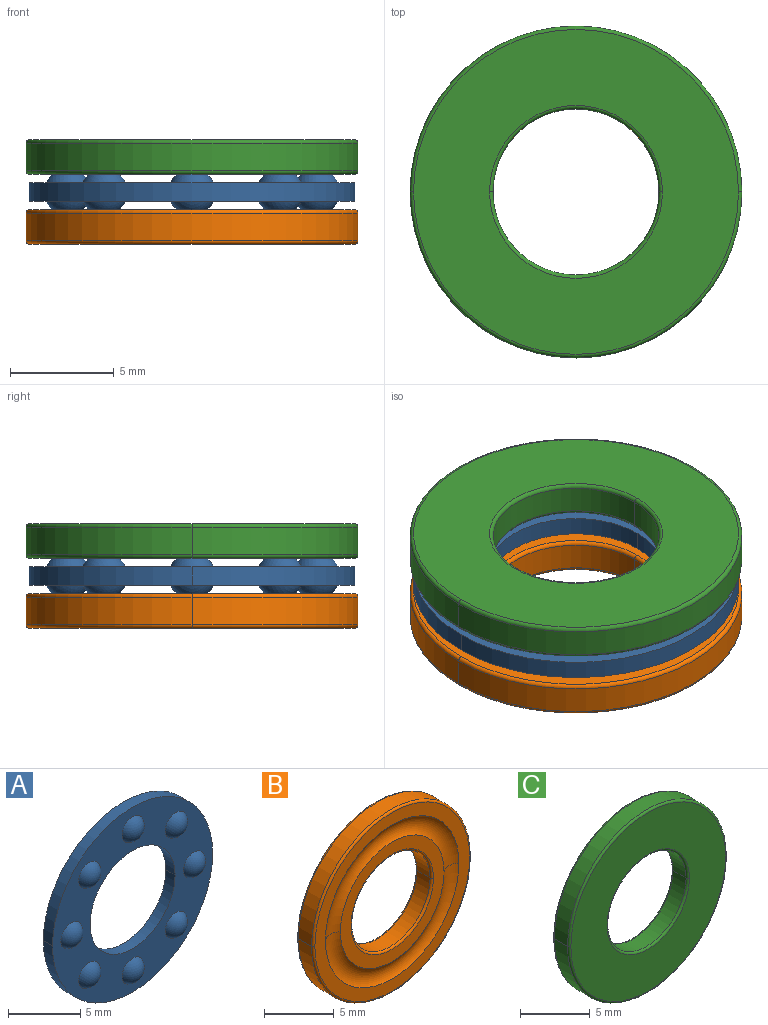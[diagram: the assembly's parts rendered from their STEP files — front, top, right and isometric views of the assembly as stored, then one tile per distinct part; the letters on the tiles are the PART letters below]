
ASSEMBLY  parts=3 mates=4
PART A: 22 faces, bbox 15.7x2.3x15.7 mm
  f0: sphere r=1.12mm, area 4.8mm2, adj f19
  f1: sphere r=1.12mm, area 4.8mm2, adj f19
  f2: sphere r=1.12mm, area 4.8mm2, adj f19
  f3: sphere r=1.12mm, area 4.8mm2, adj f19
  f4: sphere r=1.12mm, area 4.8mm2, adj f19
  f5: sphere r=1.12mm, area 4.8mm2, adj f19
  f6: sphere r=1.12mm, area 4.8mm2, adj f19
  f7: sphere r=1.12mm, area 4.8mm2, adj f19
  f8: sphere r=1.12mm, area 4.8mm2, adj f16
  f9: sphere r=1.12mm, area 4.8mm2, adj f16
  f10: sphere r=1.12mm, area 4.8mm2, adj f16
  f11: sphere r=1.12mm, area 4.8mm2, adj f16
  f12: sphere r=1.12mm, area 4.8mm2, adj f16
  f13: sphere r=1.12mm, area 4.8mm2, adj f16
  f14: sphere r=1.12mm, area 4.8mm2, adj f16
  f15: sphere r=1.12mm, area 4.8mm2, adj f16
  f16: plane 15.68x15.68mm, normal (0,1,0), area 112mm2, adj f8,f9,f10,f11,f12,f13,f14,f15
  f17: cylinder r=4.16mm len=8.32mm, axis (0,-1,0), area 11.8mm2, adj f16,f18,f19
  f18: cylinder r=4.16mm len=8.32mm, axis (0,-1,0), area 11.8mm2, adj f16,f17,f19
  f19: plane 15.68x15.68mm, normal (0,-1,0), area 112mm2, adj f0,f1,f2,f3,f4,f5,f6,f7
  f20: cylinder r=7.84mm len=15.68mm, axis (0,-1,0), area 22.2mm2, adj f16,f19,f21
  f21: cylinder r=7.84mm len=15.68mm, axis (0,-1,0), area 22.2mm2, adj f16,f19,f20
PART B: 306 faces, bbox 17.3x1.7x17.3 mm
  f0: plane 1.01x0.83mm, normal (0,1,0), area 0.3mm2, adj f1,f2,f3,f4,f5,f6,f7,f8
  f1: plane 0.15x0.07mm, normal (0,0,-1), area 0mm2, adj f0,f2,f54,f304
  f2: plane 0.15x0.1mm, normal (-0.31,0,-0.95), area 0mm2, adj f0,f1,f3,f304
  f3: plane 0.15x0.09mm, normal (-0.57,0,-0.82), area 0mm2, adj f0,f2,f4,f304
  f4: plane 0.15x0.09mm, normal (-0.87,0,-0.49), area 0mm2, adj f0,f3,f5,f304
  f5: plane 0.15x0.1mm, normal (-0.95,0,-0.31), area 0mm2, adj f0,f4,f6,f304
  f6: plane 0.15x0.09mm, normal (-1,0,-0.06), area 0mm2, adj f0,f5,f7,f304
  f7: plane 0.15x0.09mm, normal (-0.99,0,0.16), area 0mm2, adj f0,f6,f8,f304
  f8: plane 0.15x0.11mm, normal (-0.89,0,0.46), area 0mm2, adj f0,f7,f9,f304
  f9: plane 0.15x0.07mm, normal (-0.53,0,0.85), area 0mm2, adj f0,f8,f10,f304
  f10: plane 0.15x0.08mm, normal (-0.31,0,0.95), area 0mm2, adj f0,f9,f11,f304
  f11: plane 0.15x0.09mm, normal (-0.07,0,1), area 0mm2, adj f0,f10,f12,f304
  f12: plane 0.15x0.11mm, normal (0.45,0,0.9), area 0mm2, adj f0,f11,f13,f304
  f13: plane 0.15x0.07mm, normal (0.71,0,0.71), area 0mm2, adj f0,f12,f14,f304
  f14: plane 0.15x0.07mm, normal (0.85,0,0.53), area 0mm2, adj f0,f13,f15,f304
  f15: plane 0.15x0.12mm, normal (0.95,0,0.31), area 0mm2, adj f0,f14,f16,f304
  f16: plane 0.15x0.07mm, normal (0.85,0,0.53), area 0mm2, adj f0,f15,f17,f304
  f17: plane 0.15x0.06mm, normal (0.61,0,0.79), area 0mm2, adj f0,f16,f18,f304
  f18: plane 0.15x0.07mm, normal (0.26,0,0.97), area 0mm2, adj f0,f17,f19,f304
  f19: plane 0.15x0.06mm, normal (-0.31,0,0.95), area 0mm2, adj f0,f18,f20,f304
  f20: plane 0.15x0.06mm, normal (-0.78,0,0.63), area 0mm2, adj f0,f19,f21,f304
  f21: plane 0.15x0.07mm, normal (-0.96,0,0.28), area 0mm2, adj f0,f20,f22,f304
  f22: plane 0.15x0.09mm, normal (-1,0,-0.06), area 0mm2, adj f0,f21,f23,f304
  f23: plane 0.16x0.15mm, normal (-0.95,0,-0.31), area 0mm2, adj f0,f22,f24,f304
  f24: plane 0.15x0.07mm, normal (-0.85,0,-0.53), area 0mm2, adj f0,f23,f25,f304
  f25: plane 0.15x0.08mm, normal (-0.45,0,-0.9), area 0mm2, adj f0,f24,f26,f304
  f26: plane 0.15x0.07mm, normal (0,0,-1), area 0mm2, adj f0,f25,f27,f304
  f27: plane 0.15x0.12mm, normal (-0.95,0,-0.31), area 0mm2, adj f0,f26,f28,f304
  f28: plane 0.15x0.09mm, normal (-0.07,0,1), area 0mm2, adj f0,f27,f29,f304
  f29: plane 0.15x0.12mm, normal (0.22,0,0.98), area 0mm2, adj f0,f28,f30,f304
  f30: plane 0.15x0.09mm, normal (0.65,0,0.76), area 0mm2, adj f0,f29,f31,f304
  f31: plane 0.15x0.09mm, normal (0.87,0,0.49), area 0mm2, adj f0,f30,f32,f304
  f32: plane 0.16x0.15mm, normal (0.95,0,0.31), area 0mm2, adj f0,f31,f33,f304
  f33: plane 0.15x0.11mm, normal (0.99,0,0.11), area 0mm2, adj f0,f32,f34,f304
  f34: plane 0.15x0.09mm, normal (0.99,0,-0.16), area 0mm2, adj f0,f33,f35,f304
  f35: plane 0.15x0.11mm, normal (0.89,0,-0.46), area 0mm2, adj f0,f34,f36,f304
  f36: plane 0.15x0.07mm, normal (0.7,0,-0.72), area 0mm2, adj f0,f35,f37,f304
  f37: plane 0.15x0.1mm, normal (0.31,0,-0.95), area 0mm2, adj f0,f36,f38,f304
  f38: plane 0.15x0.09mm, normal (-0.14,0,-0.99), area 0mm2, adj f0,f37,f39,f304
  f39: plane 0.15x0.11mm, normal (-0.45,0,-0.9), area 0mm2, adj f0,f38,f40,f304
  f40: plane 0.15x0.07mm, normal (-0.71,0,-0.71), area 0mm2, adj f0,f39,f41,f304
  f41: plane 0.15x0.09mm, normal (-0.87,0,-0.49), area 0mm2, adj f0,f40,f42,f304
  f42: plane 0.15x0.12mm, normal (-0.95,0,-0.31), area 0mm2, adj f0,f41,f43,f304
  f43: plane 0.15x0.05mm, normal (-0.8,0,-0.6), area 0mm2, adj f0,f42,f44,f304
  f44: plane 0.15x0.06mm, normal (-0.61,0,-0.79), area 0mm2, adj f0,f43,f45,f304
  f45: plane 0.15x0.07mm, normal (0,0,-1), area 0mm2, adj f0,f44,f46,f304
  f46: plane 0.15x0.04mm, normal (0.31,0,-0.95), area 0mm2, adj f0,f45,f47,f304
  f47: plane 0.15x0.05mm, normal (0.59,0,-0.81), area 0mm2, adj f0,f46,f48,f304
  f48: plane 0.15x0.07mm, normal (0.96,0,-0.28), area 0mm2, adj f0,f47,f49,f304
  f49: plane 0.15x0.07mm, normal (1,0,-0.01), area 0mm2, adj f0,f48,f50,f304
  f50: plane 0.15x0.12mm, normal (0.95,0,0.31), area 0mm2, adj f0,f49,f51,f304
  f51: plane 0.15x0.05mm, normal (0.8,0,0.6), area 0mm2, adj f0,f50,f52,f304
  f52: plane 0.15x0.05mm, normal (0.45,0,0.9), area 0mm2, adj f0,f51,f53,f304
  f53: plane 0.15x0.05mm, normal (0.14,0,0.99), area 0mm2, adj f0,f52,f54,f304
  f54: plane 0.15x0.12mm, normal (0.95,0,0.31), area 0mm2, adj f0,f1,f53,f304
  f55: plane 0.31x0.15mm, normal (-0.99,0,-0.14), area 0mm2, adj f56,f60,f98,f304
  f56: plane 0.15x0.13mm, normal (-0.14,0,0.99), area 0mm2, adj f55,f57,f60,f304
  f57: plane 0.19x0.15mm, normal (0.99,0,0.14), area 0mm2, adj f56,f58,f60,f304
  f58: plane 0.17x0.15mm, normal (-0.14,0,0.99), area 0mm2, adj f57,f59,f60,f304
  f59: plane 0.15x0.06mm, normal (-0.44,0,0.9), area 0mm2, adj f58,f60,f304,f305
  f60: plane 1.02x0.86mm, normal (0,1,0), area 0.3mm2, adj f55,f56,f57,f58,f59,f61,f62,f63
  f61: plane 0.15x0.09mm, normal (-0.99,0,0.11), area 0mm2, adj f60,f62,f304,f305
  f62: plane 0.19x0.15mm, normal (-0.99,0,-0.14), area 0mm2, adj f60,f61,f63,f304
  f63: plane 0.15x0.08mm, normal (-0.93,0,-0.38), area 0mm2, adj f60,f62,f64,f304
  f64: plane 0.15x0.06mm, normal (-0.74,0,-0.67), area 0mm2, adj f60,f63,f65,f304
  f65: plane 0.15x0.07mm, normal (-0.42,0,-0.91), area 0mm2, adj f60,f64,f66,f304
  f66: plane 0.15x0.09mm, normal (-0.1,0,-0.99), area 0mm2, adj f60,f65,f67,f304
  f67: plane 0.32x0.15mm, normal (0.14,0,-0.99), area 0mm2, adj f60,f66,f68,f304
  f68: plane 0.15x0.08mm, normal (0.37,0,-0.93), area 0mm2, adj f60,f67,f69,f304
  f69: plane 0.15x0.06mm, normal (0.66,0,-0.75), area 0mm2, adj f60,f68,f70,f304
  f70: plane 0.15x0.07mm, normal (0.9,0,-0.44), area 0mm2, adj f60,f69,f71,f304
  f71: plane 0.15x0.09mm, normal (0.99,0,-0.11), area 0mm2, adj f60,f70,f72,f304
  f72: plane 0.19x0.15mm, normal (0.99,0,0.14), area 0mm2, adj f60,f71,f73,f304
  f73: plane 0.15x0.08mm, normal (0.93,0,0.38), area 0mm2, adj f60,f72,f74,f304
  f74: plane 0.15x0.06mm, normal (0.74,0,0.67), area 0mm2, adj f60,f73,f75,f304
  f75: plane 0.15x0.07mm, normal (0.18,0,0.98), area 0mm2, adj f60,f74,f76,f304
  f76: plane 0.15x0.12mm, normal (0.99,0,0.14), area 0mm2, adj f60,f75,f77,f304
  f77: plane 0.15x0.11mm, normal (-0.05,0,-1), area 0mm2, adj f60,f76,f78,f304
  f78: plane 0.15x0.1mm, normal (-0.59,0,-0.8), area 0mm2, adj f60,f77,f79,f304
  f79: plane 0.15x0.08mm, normal (-0.82,0,-0.57), area 0mm2, adj f60,f78,f80,f304
  f80: plane 0.15x0.1mm, normal (-0.94,0,-0.33), area 0mm2, adj f60,f79,f81,f304
  f81: plane 0.19x0.15mm, normal (-0.99,0,-0.14), area 0mm2, adj f60,f80,f82,f304
  f82: plane 0.15x0.11mm, normal (-1,0,0.06), area 0mm2, adj f60,f81,f83,f304
  f83: plane 0.15x0.09mm, normal (-0.95,0,0.33), area 0mm2, adj f60,f82,f84,f304
  f84: plane 0.15x0.09mm, normal (-0.79,0,0.61), area 0mm2, adj f60,f83,f85,f304
  f85: plane 0.15x0.08mm, normal (-0.56,0,0.83), area 0mm2, adj f60,f84,f86,f304
  f86: plane 0.15x0.1mm, normal (-0.33,0,0.95), area 0mm2, adj f60,f85,f87,f304
  f87: plane 0.32x0.15mm, normal (-0.14,0,0.99), area 0mm2, adj f60,f86,f88,f304
  f88: plane 0.15x0.11mm, normal (0.05,0,1), area 0mm2, adj f60,f87,f89,f304
  f89: plane 0.15x0.09mm, normal (0.31,0,0.95), area 0mm2, adj f60,f88,f90,f304
  f90: plane 0.15x0.1mm, normal (0.59,0,0.8), area 0mm2, adj f60,f89,f91,f304
  f91: plane 0.15x0.08mm, normal (0.82,0,0.57), area 0mm2, adj f60,f90,f92,f304
  f92: plane 0.15x0.1mm, normal (0.94,0,0.33), area 0mm2, adj f60,f91,f93,f304
  f93: plane 0.19x0.15mm, normal (0.99,0,0.14), area 0mm2, adj f60,f92,f94,f304
  f94: plane 0.15x0.11mm, normal (1,0,-0.06), area 0mm2, adj f60,f93,f95,f304
  f95: plane 0.15x0.09mm, normal (0.95,0,-0.33), area 0mm2, adj f60,f94,f96,f304
  f96: plane 0.15x0.09mm, normal (0.79,0,-0.61), area 0mm2, adj f60,f95,f97,f304
  f97: plane 0.15x0.08mm, normal (0.37,0,-0.93), area 0mm2, adj f60,f96,f98,f304
  f98: plane 0.32x0.15mm, normal (0.14,0,-0.99), area 0mm2, adj f55,f60,f97,f304
  f99: plane 1.03x0.87mm, normal (0,1,0), area 0.4mm2, adj f100,f101,f102,f103,f104,f105,f106,f107
  f100: plane 0.85x0.56mm, normal (0.55,0,0.84), area 0.2mm2, adj f99,f101,f109,f304
  f101: plane 0.19x0.15mm, normal (1,0,-0.04), area 0mm2, adj f99,f100,f102,f304
  f102: plane 1x0.15mm, normal (-0.04,0,-1), area 0.1mm2, adj f99,f101,f103,f304
  f103: plane 0.15x0.13mm, normal (-1,0,0.04), area 0mm2, adj f99,f102,f104,f304
  f104: plane 0.85x0.15mm, normal (0.04,0,1), area 0.1mm2, adj f99,f103,f105,f304
  f105: plane 0.83x0.56mm, normal (-0.56,0,-0.83), area 0.1mm2, adj f99,f104,f106,f304
  f106: plane 0.19x0.15mm, normal (-1,0,0.04), area 0mm2, adj f99,f105,f107,f304
  f107: plane 1x0.15mm, normal (0.04,0,1), area 0.1mm2, adj f99,f106,f108,f304
  f108: plane 0.15x0.13mm, normal (1,0,-0.04), area 0mm2, adj f99,f107,f109,f304
  f109: plane 0.87x0.15mm, normal (-0.04,0,-1), area 0.1mm2, adj f99,f100,f108,f304
  f110: plane 1.01x0.28mm, normal (0,1,0), area 0.1mm2, adj f111,f112,f113,f114
  f111: plane 0.15x0.12mm, normal (-0.99,0,0.16), area 0mm2, adj f110,f112,f114,f304
  f112: plane 0.99x0.16mm, normal (0.16,0,0.99), area 0.2mm2, adj f110,f111,f113,f304
  f113: plane 0.15x0.12mm, normal (0.99,0,-0.16), area 0mm2, adj f110,f112,f114,f304
  f114: plane 0.99x0.16mm, normal (-0.16,0,-0.99), area 0.2mm2, adj f110,f111,f113,f304
  f115: plane 0.15x0.05mm, normal (-0.83,0,0.56), area 0mm2, adj f116,f124,f125,f126
  f116: plane 0.15x0.05mm, normal (-0.48,0,0.88), area 0mm2, adj f115,f117,f124,f126
  f117: plane 0.15x0.07mm, normal (-0.04,0,1), area 0mm2, adj f116,f118,f124,f126
  f118: plane 0.15x0.06mm, normal (0.27,0,0.96), area 0mm2, adj f117,f119,f124,f126
  f119: plane 0.15x0.06mm, normal (0.55,0,0.83), area 0mm2, adj f118,f120,f124,f126
  f120: plane 0.15x0.05mm, normal (0.87,0,0.5), area 0mm2, adj f119,f121,f124,f126
  f121: plane 0.15x0.07mm, normal (1,0,0.06), area 0mm2, adj f120,f122,f124,f126
  f122: plane 0.38x0.15mm, normal (0.96,0,-0.27), area 0.1mm2, adj f121,f123,f124,f126
  f123: plane 0.31x0.15mm, normal (-0.27,0,-0.96), area 0mm2, adj f122,f124,f125,f126
  f124: plane 0.55x0.41mm, normal (0,1,0), area 0.2mm2, adj f115,f116,f117,f118,f119,f120,f121,f122
  f125: plane 0.38x0.15mm, normal (-0.96,0,0.27), area 0.1mm2, adj f115,f123,f124,f126
  f126: plane 1.11x1.03mm, normal (0,1,0), area 0.4mm2, adj f115,f116,f117,f118,f119,f120,f121,f122
  f127: plane 0.39x0.28mm, normal (0.59,0,0.81), area 0.1mm2, adj f126,f128,f142,f304
  f128: plane 0.15x0.14mm, normal (0.96,0,-0.27), area 0mm2, adj f126,f127,f129,f304
  f129: plane 0.42x0.31mm, normal (-0.6,0,-0.8), area 0.1mm2, adj f126,f128,f130,f304
  f130: plane 0.15x0.07mm, normal (0.74,0,-0.68), area 0mm2, adj f126,f129,f131,f304
  f131: plane 0.15x0.1mm, normal (0.35,0,-0.94), area 0mm2, adj f126,f130,f132,f304
  f132: plane 0.15x0.07mm, normal (0.04,0,-1), area 0mm2, adj f126,f131,f133,f304
  f133: plane 0.15x0.08mm, normal (-0.27,0,-0.96), area 0mm2, adj f126,f132,f134,f304
  f134: plane 0.15x0.06mm, normal (-0.55,0,-0.83), area 0mm2, adj f126,f133,f135,f304
  f135: plane 0.15x0.08mm, normal (-0.79,0,-0.62), area 0mm2, adj f126,f134,f136,f304
  f136: plane 0.15x0.1mm, normal (-0.93,0,-0.37), area 0mm2, adj f126,f135,f137,f304
  f137: plane 0.15x0.11mm, normal (-1,0,0.07), area 0mm2, adj f126,f136,f138,f304
  f138: plane 0.48x0.15mm, normal (-0.96,0,0.27), area 0.1mm2, adj f126,f137,f139,f304
  f139: plane 0.96x0.27mm, normal (0.27,0,0.96), area 0.1mm2, adj f126,f138,f140,f304
  f140: plane 0.15x0.12mm, normal (0.96,0,-0.27), area 0mm2, adj f126,f139,f141,f304
  f141: plane 0.43x0.15mm, normal (-0.27,0,-0.96), area 0.1mm2, adj f126,f140,f142,f304
  f142: plane 0.34x0.15mm, normal (0.96,0,-0.27), area 0.1mm2, adj f126,f127,f141,f304
  f143: plane 0.6x0.15mm, normal (-0.13,0,-0.99), area 0.1mm2, adj f144,f145,f146,f147
  f144: plane 0.34x0.16mm, normal (-0.9,0,0.43), area 0.1mm2, adj f143,f145,f146,f147
  f145: plane 0.6x0.42mm, normal (0,1,0), area 0.1mm2, adj f143,f144,f146
  f146: plane 0.44x0.42mm, normal (0.69,0,0.72), area 0.1mm2, adj f143,f144,f145,f147
  f147: plane 1.12x0.89mm, normal (0,1,0), area 0.3mm2, adj f143,f144,f146,f148,f149,f150,f151,f152
  f148: plane 1.05x0.15mm, normal (0.13,0,0.99), area 0.2mm2, adj f147,f149,f155,f304
  f149: plane 0.15x0.11mm, normal (0.9,0,-0.43), area 0mm2, adj f147,f148,f150,f304
  f150: plane 0.27x0.15mm, normal (-0.13,0,-0.99), area 0mm2, adj f147,f149,f151,f304
  f151: plane 0.38x0.18mm, normal (0.9,0,-0.43), area 0.1mm2, adj f147,f150,f152,f304
  f152: plane 0.19x0.19mm, normal (0.69,0,0.72), area 0mm2, adj f147,f151,f153,f304
  f153: plane 0.15x0.11mm, normal (0.9,0,-0.43), area 0mm2, adj f147,f152,f154,f304
  f154: plane 0.76x0.74mm, normal (-0.7,0,-0.72), area 0.2mm2, adj f147,f153,f155,f304
  f155: plane 0.15x0.15mm, normal (-0.9,0,0.43), area 0mm2, adj f147,f148,f154,f304
  f156: plane 1.25x1.19mm, normal (0,1,0), area 0.4mm2, adj f157,f158,f159,f160,f161,f162,f163,f164
  f157: plane 0.28x0.2mm, normal (-0.58,0,-0.81), area 0.1mm2, adj f156,f158,f168,f304
  f158: plane 0.44x0.32mm, normal (0.81,0,-0.58), area 0.1mm2, adj f156,f157,f159,f304
  f159: plane 0.15x0.1mm, normal (-0.58,0,-0.81), area 0mm2, adj f156,f158,f160,f304
  f160: plane 0.44x0.32mm, normal (-0.81,0,0.58), area 0.1mm2, adj f156,f159,f161,f304
  f161: plane 0.22x0.16mm, normal (-0.58,0,-0.81), area 0mm2, adj f156,f160,f162,f304
  f162: plane 0.51x0.37mm, normal (0.81,0,-0.58), area 0.1mm2, adj f156,f161,f163,f304
  f163: plane 0.15x0.1mm, normal (-0.58,0,-0.81), area 0mm2, adj f156,f162,f164,f304
  f164: plane 0.61x0.44mm, normal (-0.81,0,0.58), area 0.1mm2, adj f156,f163,f165,f304
  f165: plane 0.81x0.58mm, normal (0.58,0,0.81), area 0.2mm2, adj f156,f164,f166,f304
  f166: plane 0.61x0.44mm, normal (0.81,0,-0.58), area 0.1mm2, adj f156,f165,f167,f304
  f167: plane 0.15x0.1mm, normal (-0.58,0,-0.81), area 0mm2, adj f156,f166,f168,f304
  f168: plane 0.51x0.37mm, normal (-0.81,0,0.58), area 0.1mm2, adj f156,f157,f167,f304
  f169: plane 0.15x0.06mm, normal (0.89,0,0.45), area 0mm2, adj f170,f178,f179,f191
  f170: plane 0.15x0.06mm, normal (1,0,0), area 0mm2, adj f169,f171,f178,f191
  f171: plane 0.15x0.06mm, normal (0.89,0,-0.45), area 0mm2, adj f170,f172,f178,f191
  f172: plane 0.28x0.28mm, normal (0.7,0,-0.71), area 0.1mm2, adj f171,f173,f178,f191
  f173: plane 0.23x0.22mm, normal (-0.71,0,-0.7), area 0mm2, adj f172,f174,f178,f191
  f174: plane 0.28x0.28mm, normal (-0.7,0,0.71), area 0.1mm2, adj f173,f175,f178,f191
  f175: plane 0.15x0.06mm, normal (-0.44,0,0.9), area 0mm2, adj f174,f176,f178,f191
  f176: plane 0.15x0.06mm, normal (0.02,0,1), area 0mm2, adj f175,f177,f178,f191
  f177: plane 0.15x0.06mm, normal (0.46,0,0.89), area 0mm2, adj f176,f178,f179,f191
  f178: plane 0.54x0.53mm, normal (0,1,0), area 0.2mm2, adj f169,f170,f171,f172,f173,f174,f175,f176
  f179: plane 0.15x0.05mm, normal (0.71,0,0.7), area 0mm2, adj f169,f177,f178,f191
  f180: plane 0.21x0.21mm, normal (-0.71,0,-0.7), area 0mm2, adj f181,f189,f190,f191
  f181: plane 0.28x0.28mm, normal (-0.7,0,0.71), area 0.1mm2, adj f180,f182,f189,f191
  f182: plane 0.15x0.06mm, normal (-0.44,0,0.9), area 0mm2, adj f181,f183,f189,f191
  f183: plane 0.15x0.06mm, normal (0.02,0,1), area 0mm2, adj f182,f184,f189,f191
  f184: plane 0.15x0.06mm, normal (0.46,0,0.89), area 0mm2, adj f183,f185,f189,f191
  f185: plane 0.15x0.03mm, normal (0.71,0,0.7), area 0mm2, adj f184,f186,f189,f191
  f186: plane 0.15x0.06mm, normal (0.89,0,0.45), area 0mm2, adj f185,f187,f189,f191
  f187: plane 0.15x0.06mm, normal (1,0,0), area 0mm2, adj f186,f188,f189,f191
  f188: plane 0.15x0.06mm, normal (0.89,0,-0.45), area 0mm2, adj f187,f189,f190,f191
  f189: plane 0.52x0.52mm, normal (0,1,0), area 0.1mm2, adj f180,f181,f182,f183,f184,f185,f186,f187
  f190: plane 0.28x0.28mm, normal (0.7,0,-0.71), area 0.1mm2, adj f180,f188,f189,f191
  f191: plane 1.13x1.13mm, normal (0,1,0), area 0.4mm2, adj f169,f170,f171,f172,f173,f174,f175,f176
  f192: plane 0.15x0.1mm, normal (-0.16,0,-0.99), area 0mm2, adj f191,f193,f210,f304
  f193: plane 0.15x0.06mm, normal (-0.46,0,-0.89), area 0mm2, adj f191,f192,f194,f304
  f194: plane 0.15x0.06mm, normal (-0.71,0,-0.7), area 0mm2, adj f191,f193,f195,f304
  f195: plane 0.15x0.06mm, normal (-0.89,0,-0.45), area 0mm2, adj f191,f194,f196,f304
  f196: plane 0.15x0.1mm, normal (-0.99,0,-0.14), area 0mm2, adj f191,f195,f197,f304
  f197: plane 0.15x0.1mm, normal (-0.99,0,0.14), area 0mm2, adj f191,f196,f198,f304
  f198: plane 0.15x0.09mm, normal (-0.83,0,0.56), area 0mm2, adj f191,f197,f199,f304
  f199: plane 0.36x0.35mm, normal (-0.7,0,0.71), area 0.1mm2, adj f191,f198,f200,f304
  f200: plane 0.71x0.7mm, normal (0.71,0,0.7), area 0.1mm2, adj f191,f199,f201,f304
  f201: plane 0.36x0.35mm, normal (0.7,0,-0.71), area 0.1mm2, adj f191,f200,f202,f304
  f202: plane 0.15x0.09mm, normal (0.55,0,-0.84), area 0mm2, adj f191,f201,f203,f304
  f203: plane 0.15x0.1mm, normal (0.12,0,-0.99), area 0mm2, adj f191,f202,f204,f304
  f204: plane 0.15x0.1mm, normal (-0.16,0,-0.99), area 0mm2, adj f191,f203,f205,f304
  f205: plane 0.15x0.06mm, normal (-0.46,0,-0.89), area 0mm2, adj f191,f204,f206,f304
  f206: plane 0.15x0.08mm, normal (-0.71,0,-0.7), area 0mm2, adj f191,f205,f207,f304
  f207: plane 0.15x0.06mm, normal (-0.89,0,-0.45), area 0mm2, adj f191,f206,f208,f304
  f208: plane 0.15x0.1mm, normal (-0.99,0,-0.14), area 0mm2, adj f191,f207,f209,f304
  f209: plane 0.15x0.04mm, normal (-0.95,0,0.31), area 0mm2, adj f191,f208,f210,f304
  f210: plane 0.15x0.04mm, normal (0.3,0,-0.95), area 0mm2, adj f191,f192,f209,f304
  f211: plane 1.1x0.83mm, normal (0,1,0), area 0.2mm2, adj f212,f213,f214,f215,f216,f217,f218,f219
  f212: plane 0.15x0.1mm, normal (0.91,0,0.41), area 0mm2, adj f211,f213,f219,f304
  f213: plane 0.3x0.15mm, normal (0.41,0,-0.91), area 0mm2, adj f211,f212,f214,f304
  f214: plane 0.81x0.37mm, normal (0.91,0,0.41), area 0.1mm2, adj f211,f213,f215,f304
  f215: plane 0.15x0.11mm, normal (0.41,0,-0.91), area 0mm2, adj f211,f214,f216,f304
  f216: plane 0.81x0.37mm, normal (-0.91,0,-0.41), area 0.1mm2, adj f211,f215,f217,f304
  f217: plane 0.3x0.15mm, normal (0.41,0,-0.91), area 0.1mm2, adj f211,f216,f218,f304
  f218: plane 0.15x0.1mm, normal (-0.91,0,-0.41), area 0mm2, adj f211,f217,f219,f304
  f219: plane 0.72x0.33mm, normal (-0.41,0,0.91), area 0.1mm2, adj f211,f212,f218,f304
  f220: plane 1.01x0.81mm, normal (0,1,0), area 0.3mm2, adj f221,f222,f223,f224,f225,f226,f227,f228
  f221: plane 0.15x0.07mm, normal (-1,0,0.06), area 0mm2, adj f220,f222,f274,f304
  f222: plane 0.15x0.1mm, normal (-0.93,0,0.37), area 0mm2, adj f220,f221,f223,f304
  f223: plane 0.15x0.08mm, normal (-0.79,0,0.62), area 0mm2, adj f220,f222,f224,f304
  f224: plane 0.15x0.1mm, normal (-0.44,0,0.9), area 0mm2, adj f220,f223,f225,f304
  f225: plane 0.15x0.1mm, normal (-0.25,0,0.97), area 0mm2, adj f220,f224,f226,f304
  f226: plane 0.15x0.09mm, normal (0,0,1), area 0mm2, adj f220,f225,f227,f304
  f227: plane 0.15x0.09mm, normal (0.22,0,0.98), area 0mm2, adj f220,f226,f228,f304
  f228: plane 0.15x0.1mm, normal (0.52,0,0.86), area 0mm2, adj f220,f227,f229,f304
  f229: plane 0.15x0.08mm, normal (0.88,0,0.47), area 0mm2, adj f220,f228,f230,f304
  f230: plane 0.15x0.08mm, normal (0.97,0,0.25), area 0mm2, adj f220,f229,f231,f304
  f231: plane 0.15x0.09mm, normal (1,0,0.01), area 0mm2, adj f220,f230,f232,f304
  f232: plane 0.15x0.1mm, normal (0.87,0,-0.5), area 0mm2, adj f220,f231,f233,f304
  f233: plane 0.15x0.07mm, normal (0.66,0,-0.75), area 0mm2, adj f220,f232,f234,f304
  f234: plane 0.15x0.08mm, normal (0.48,0,-0.88), area 0mm2, adj f220,f233,f235,f304
  f235: plane 0.15x0.12mm, normal (0.25,0,-0.97), area 0mm2, adj f220,f234,f236,f304
  f236: plane 0.15x0.08mm, normal (0.48,0,-0.88), area 0mm2, adj f220,f235,f237,f304
  f237: plane 0.15x0.06mm, normal (0.75,0,-0.66), area 0mm2, adj f220,f236,f238,f304
  f238: plane 0.15x0.07mm, normal (0.95,0,-0.32), area 0mm2, adj f220,f237,f239,f304
  f239: plane 0.15x0.06mm, normal (0.97,0,0.25), area 0mm2, adj f220,f238,f240,f304
  f240: plane 0.15x0.06mm, normal (0.67,0,0.74), area 0mm2, adj f220,f239,f241,f304
  f241: plane 0.15x0.07mm, normal (0.34,0,0.94), area 0mm2, adj f220,f240,f242,f304
  f242: plane 0.15x0.09mm, normal (0,0,1), area 0mm2, adj f220,f241,f243,f304
  f243: plane 0.16x0.15mm, normal (-0.25,0,0.97), area 0mm2, adj f220,f242,f244,f304
  f244: plane 0.15x0.08mm, normal (-0.48,0,0.88), area 0mm2, adj f220,f243,f245,f304
  f245: plane 0.15x0.08mm, normal (-0.87,0,0.5), area 0mm2, adj f220,f244,f246,f304
  f246: plane 0.15x0.07mm, normal (-1,0,0.06), area 0mm2, adj f220,f245,f247,f304
  f247: plane 0.15x0.12mm, normal (-0.25,0,0.97), area 0mm2, adj f220,f246,f248,f304
  f248: plane 0.15x0.09mm, normal (1,0,0.01), area 0mm2, adj f220,f247,f249,f304
  f249: plane 0.15x0.12mm, normal (0.96,0,-0.28), area 0mm2, adj f220,f248,f250,f304
  f250: plane 0.15x0.09mm, normal (0.72,0,-0.7), area 0mm2, adj f220,f249,f251,f304
  f251: plane 0.15x0.1mm, normal (0.44,0,-0.9), area 0mm2, adj f220,f250,f252,f304
  f252: plane 0.16x0.15mm, normal (0.25,0,-0.97), area 0mm2, adj f220,f251,f253,f304
  f253: plane 0.15x0.11mm, normal (0.05,0,-1), area 0mm2, adj f220,f252,f254,f304
  f254: plane 0.15x0.09mm, normal (-0.22,0,-0.98), area 0mm2, adj f220,f253,f255,f304
  f255: plane 0.15x0.1mm, normal (-0.52,0,-0.86), area 0mm2, adj f220,f254,f256,f304
  f256: plane 0.15x0.07mm, normal (-0.76,0,-0.65), area 0mm2, adj f220,f255,f257,f304
  f257: plane 0.15x0.1mm, normal (-0.97,0,-0.25), area 0mm2, adj f220,f256,f258,f304
  f258: plane 0.15x0.09mm, normal (-0.98,0,0.2), area 0mm2, adj f220,f257,f259,f304
  f259: plane 0.15x0.1mm, normal (-0.87,0,0.5), area 0mm2, adj f220,f258,f260,f304
  f260: plane 0.15x0.07mm, normal (-0.66,0,0.75), area 0mm2, adj f220,f259,f261,f304
  f261: plane 0.15x0.1mm, normal (-0.44,0,0.9), area 0mm2, adj f220,f260,f262,f304
  f262: plane 0.15x0.12mm, normal (-0.25,0,0.97), area 0mm2, adj f220,f261,f263,f304
  f263: plane 0.15x0.06mm, normal (-0.55,0,0.84), area 0mm2, adj f220,f262,f264,f304
  f264: plane 0.15x0.06mm, normal (-0.75,0,0.66), area 0mm2, adj f220,f263,f265,f304
  f265: plane 0.15x0.07mm, normal (-1,0,0.06), area 0mm2, adj f220,f264,f266,f304
  f266: plane 0.15x0.04mm, normal (-0.97,0,-0.25), area 0mm2, adj f220,f265,f267,f304
  f267: plane 0.15x0.06mm, normal (-0.84,0,-0.54), area 0mm2, adj f220,f266,f268,f304
  f268: plane 0.15x0.07mm, normal (-0.34,0,-0.94), area 0mm2, adj f220,f267,f269,f304
  f269: plane 0.15x0.07mm, normal (-0.08,0,-1), area 0mm2, adj f220,f268,f270,f304
  f270: plane 0.15x0.12mm, normal (0.25,0,-0.97), area 0mm2, adj f220,f269,f271,f304
  f271: plane 0.15x0.06mm, normal (0.55,0,-0.84), area 0mm2, adj f220,f270,f272,f304
  f272: plane 0.15x0.05mm, normal (0.87,0,-0.5), area 0mm2, adj f220,f271,f273,f304
  f273: plane 0.15x0.05mm, normal (0.98,0,-0.2), area 0mm2, adj f220,f272,f274,f304
  f274: plane 0.15x0.12mm, normal (0.25,0,-0.97), area 0mm2, adj f220,f221,f273,f304
  f275: plane 0.56x0.23mm, normal (-0.92,0,-0.38), area 0.1mm2, adj f276,f277,f278,f279
  f276: plane 0.37x0.15mm, normal (-0.08,0,1), area 0.1mm2, adj f275,f277,f278,f279
  f277: plane 0.59x0.37mm, normal (0,1,0), area 0.1mm2, adj f275,f276,f278
  f278: plane 0.59x0.15mm, normal (0.97,0,-0.24), area 0.1mm2, adj f275,f276,f277,f279
  f279: plane 1.04x0.83mm, normal (0,1,0), area 0.3mm2, adj f275,f276,f278,f280,f281,f282,f283,f284
  f280: plane 0.97x0.41mm, normal (0.92,0,0.39), area 0.2mm2, adj f279,f281,f287,f304
  f281: plane 0.15x0.12mm, normal (0.08,0,-1), area 0mm2, adj f279,f280,f282,f304
  f282: plane 0.25x0.15mm, normal (-0.92,0,-0.38), area 0mm2, adj f279,f281,f283,f304
  f283: plane 0.42x0.15mm, normal (0.08,0,-1), area 0.1mm2, adj f279,f282,f284,f304
  f284: plane 0.26x0.15mm, normal (0.97,0,-0.24), area 0mm2, adj f279,f283,f285,f304
  f285: plane 0.15x0.12mm, normal (0.08,0,-1), area 0mm2, adj f279,f284,f286,f304
  f286: plane 1.02x0.26mm, normal (-0.97,0,0.24), area 0.2mm2, adj f279,f285,f287,f304
  f287: plane 0.17x0.15mm, normal (-0.08,0,1), area 0mm2, adj f279,f280,f286,f304
  f288: torus R=4.17mm, axis (0,-1,0), area 3.3mm2, adj f289,f291,f304
  f289: torus R=4.17mm, axis (0,-1,0), area 3.3mm2, adj f288,f290,f304
  f290: cylinder r=4mm len=8mm, axis (0,-1,0), area 16.8mm2, adj f289,f291,f293
  f291: cylinder r=4mm len=8mm, axis (0,-1,0), area 16.8mm2, adj f288,f290,f292
  f292: torus R=4.17mm, axis (0,-1,0), area 3.3mm2, adj f291,f293,f294
  f293: torus R=4.17mm, axis (0,-1,0), area 3.3mm2, adj f290,f292,f294
  f294: plane 10.49x10.49mm, normal (0,-1,0), area 31.9mm2, adj f292,f293,f295,f296
  f295: torus R=6mm, axis (0,-1,0), area 31.2mm2, adj f294,f296,f297
  f296: torus R=6mm, axis (0,-1,0), area 31.2mm2, adj f294,f295,f297
  f297: plane 15.67x15.67mm, normal (0,-1,0), area 49.4mm2, adj f295,f296,f298,f299
  f298: torus R=7.83mm, axis (0,-1,0), area 6.5mm2, adj f297,f299,f301
  f299: torus R=7.83mm, axis (0,-1,0), area 6.5mm2, adj f297,f298,f300
  f300: cylinder r=8mm len=16mm, axis (0,-1,0), area 33.5mm2, adj f299,f301,f303
  f301: cylinder r=8mm len=16mm, axis (0,-1,0), area 33.5mm2, adj f298,f300,f302
  f302: torus R=7.83mm, axis (0,-1,0), area 6.5mm2, adj f301,f303,f304
  f303: torus R=7.83mm, axis (0,-1,0), area 6.5mm2, adj f300,f302,f304
  f304: plane 15.67x15.67mm, normal (0,1,0), area 134.3mm2, adj f1,f2,f3,f4,f5,f6,f7,f8
  f305: plane 0.15x0.07mm, normal (-0.9,0,0.44), area 0mm2, adj f59,f60,f61,f304
PART C: 17 faces, bbox 17.3x1.7x17.3 mm
  f0: plane 10.49x10.49mm, normal (0,1,0), area 31.9mm2, adj f1,f2,f15,f16
  f1: torus R=4.17mm, axis (0,-1,0), area 3.3mm2, adj f0,f2,f4
  f2: torus R=4.17mm, axis (0,-1,0), area 3.3mm2, adj f0,f1,f3
  f3: cylinder r=4mm len=8mm, axis (0,-1,0), area 16.8mm2, adj f2,f4,f6
  f4: cylinder r=4mm len=8mm, axis (0,-1,0), area 16.8mm2, adj f1,f3,f5
  f5: torus R=4.17mm, axis (0,-1,0), area 3.3mm2, adj f4,f6,f7
  f6: torus R=4.17mm, axis (0,-1,0), area 3.3mm2, adj f3,f5,f7
  f7: plane 15.67x15.67mm, normal (0,-1,0), area 138.2mm2, adj f5,f6,f8,f9
  f8: torus R=7.83mm, axis (0,-1,0), area 6.5mm2, adj f7,f9,f11
  f9: torus R=7.83mm, axis (0,-1,0), area 6.5mm2, adj f7,f8,f10
  f10: cylinder r=8mm len=16mm, axis (0,-1,0), area 33.5mm2, adj f9,f11,f13
  f11: cylinder r=8mm len=16mm, axis (0,-1,0), area 33.5mm2, adj f8,f10,f12
  f12: torus R=7.83mm, axis (0,-1,0), area 6.5mm2, adj f11,f13,f14
  f13: torus R=7.83mm, axis (0,-1,0), area 6.5mm2, adj f10,f12,f14
  f14: plane 15.67x15.67mm, normal (0,1,0), area 49.4mm2, adj f12,f13,f15,f16
  f15: torus R=6mm, axis (0,-1,0), area 31.2mm2, adj f0,f14,f16
  f16: torus R=6mm, axis (0,-1,0), area 31.2mm2, adj f0,f14,f15
PLACE A rot(axis=(-1,0,0),90deg) t=(-4.04,-4.48,-2.01)mm
PLACE B rot(axis=(-1,0,0),90deg) t=(-4.04,-4.48,-2.03)mm
PLACE C rot(axis=(-1,0,0),90deg) t=(-4.04,-4.48,-2)mm
MATE planar C.f1 <-> A.f17  axis (0,0,-1) through (-4.04,-4.48,-1.16)mm
MATE planar A.f17 <-> B.f288  axis (0,0,-1) through (-4.04,-4.48,-2.46)mm
MATE slider C.f1 <-> B.f288  axis (0,0,1) through (-4.04,-4.48,-0.33)mm
MATE slider C.f1 <-> A.f17  axis (0,0,1) through (-4.04,-4.48,-0.33)mm
